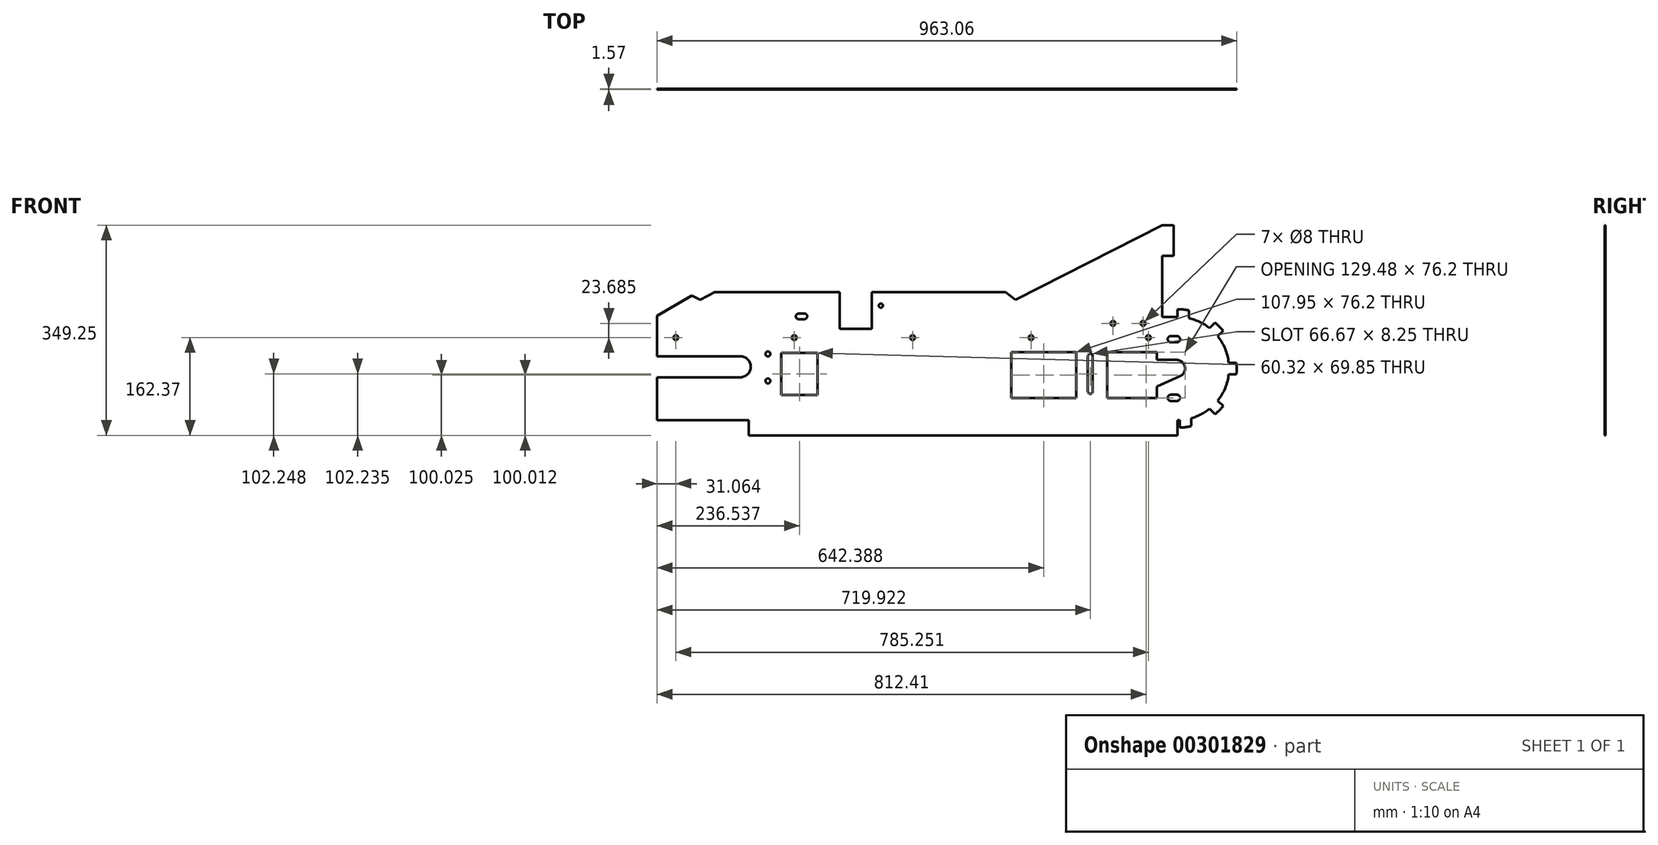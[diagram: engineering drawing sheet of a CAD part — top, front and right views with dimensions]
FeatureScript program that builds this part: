
annotation { "Feature Type Name" : "Feature", "Feature Type Description" : "" }
export const myFeature = defineFeature(function(context is Context, id is Id, definition is map)
    precondition{}
    {
        {
            var Q0;
            Q0=qCreatedBy(makeId("Front.planeOp"),FACE);
            var sketch = newSketch(context, id + "F0", { "sketchPlane" : qUnion([Q0])});
            skLineSegment(sketch, "E0", {"start": v(0, 0) * mm, "end": v(864.64, 0) * mm});
            skLineSegment(sketch, "E1", {"start": v(0, 71.12) * mm, "end": v(138.11, 71.12) * mm});
            skLineSegment(sketch, "E2", {"start": v(138.11, 106.05) * mm, "end": v(0, 106.05) * mm});
            skLineSegment(sketch, "E3", {"start": v(0, 106.05) * mm, "end": v(0, 158.75) * mm});
            skLineSegment(sketch, "E4", {"start": v(0, 158.75) * mm, "end": v(71.5, 200.03) * mm});
            skLineSegment(sketch, "E5", {"start": v(71.5, 200.03) * mm, "end": v(303.21, 200.03) * mm});
            skLineSegment(sketch, "E6", {"start": v(839.24, 323.85) * mm, "end": v(839.24, 171.45) * mm});
            skPoint(sketch, "E7", {"position": v(864.64, 85.73) * mm});
            skArc(sketch, "E8", {"start": v(864.64, 0) * mm, "mid": v(950.36, 85.73) * mm, "end": v(864.64, 171.45) * mm});
            skLineSegment(sketch, "E9", {"start": v(864.64, 171.45) * mm, "end": v(749.53, 171.45) * mm});
            skPoint(sketch, "E10", {"position": v(138.11, 88.58) * mm});
            skPoint(sketch, "E10.positionSnap0", {"position": v(155.58, 88.58) * mm});
            skArc(sketch, "E11", {"start": v(138.11, 71.12) * mm, "mid": v(155.58, 88.58) * mm, "end": v(138.11, 106.04) * mm});
            skLineSegment(sketch, "E12", {"start": v(206.38, 88.58) * mm, "end": v(206.38, 41.91) * mm});
            skLineSegment(sketch, "E13", {"start": v(206.38, 41.91) * mm, "end": v(266.7, 41.91) * mm});
            skLineSegment(sketch, "E14", {"start": v(266.7, 41.91) * mm, "end": v(266.7, 111.76) * mm});
            skLineSegment(sketch, "E15", {"start": v(266.7, 111.76) * mm, "end": v(206.38, 111.76) * mm});
            skLineSegment(sketch, "E16", {"start": v(206.38, 111.76) * mm, "end": v(206.38, 88.58) * mm});
            skLineSegment(sketch, "E17", {"start": v(0, 0) * mm, "end": v(0, 71.12) * mm});
            skPoint(sketch, "E18.orphan", {"position": v(155.58, 106.05) * mm});
            skPoint(sketch, "E19.orphan", {"position": v(155.57, 71.12) * mm});
            skLineSegment(sketch, "E20.bottom", {"start": v(747.67, 36.51) * mm, "end": v(830.22, 36.51) * mm});
            skLineSegment(sketch, "E20.top", {"start": v(747.67, 112.71) * mm, "end": v(830.22, 112.71) * mm});
            skLineSegment(sketch, "E20.left", {"start": v(747.67, 36.51) * mm, "end": v(747.67, 112.71) * mm});
            skLineSegment(sketch, "E20.right", {"start": v(830.22, 36.51) * mm, "end": v(830.22, 55.56) * mm});
            skLineSegment(sketch, "E21", {"start": v(830.22, 100.01) * mm, "end": v(862.98, 100.01) * mm});
            skPoint(sketch, "E22", {"position": v(830.22, 55.56) * mm});
            skPoint(sketch, "E23", {"position": v(862.98, 85.73) * mm});
            skArc(sketch, "E24", {"start": v(868.78, 72.66) * mm, "mid": v(876.96, 88.69) * mm, "end": v(862.98, 100.01) * mm});
            skLineSegment(sketch, "E25", {"start": v(830.22, 55.56) * mm, "end": v(868.78, 72.66) * mm});
            skLineSegment(sketch, "E26.trimOffspring", {"start": v(830.22, 100.01) * mm, "end": v(830.22, 112.71) * mm});
            skLineSegment(sketch, "E27", {"start": v(152.4, 0) * mm, "end": v(152.4, -25.4) * mm});
            skLineSegment(sketch, "E28", {"start": v(152.4, -25.4) * mm, "end": v(864.64, -25.4) * mm});
            skLineSegment(sketch, "E29", {"start": v(864.64, -25.4) * mm, "end": v(864.64, 0) * mm});
            skLineSegment(sketch, "E30", {"start": v(71.5, 200.03) * mm, "end": v(95.54, 212.72) * mm});
            skLineSegment(sketch, "E31", {"start": v(95.54, 212.72) * mm, "end": v(303.21, 212.72) * mm});
            skArc(sketch, "E32.0", {"start": v(868.87, -12.6) * mm, "mid": v(878.37, -11.74) * mm, "end": v(887.74, -9.95) * mm});
            skLineSegment(sketch, "E33", {"start": v(864.64, 184.15) * mm, "end": v(864.64, 171.45) * mm});
            skLineSegment(sketch, "E34", {"start": v(883.57, 169.33) * mm, "end": v(883.6, 182.3) * mm});
            skLineSegment(sketch, "E35", {"start": v(949.83, 95.25) * mm, "end": v(962.6, 95.25) * mm});
            skLineSegment(sketch, "E36", {"start": v(949.83, 76.2) * mm, "end": v(962.6, 76.2) * mm});
            skLineSegment(sketch, "E37", {"start": v(868.87, 0.1) * mm, "end": v(868.87, -12.6) * mm});
            skLineSegment(sketch, "E38", {"start": v(887.68, 3.15) * mm, "end": v(887.74, -9.95) * mm});
            skLineSegment(sketch, "E39", {"start": v(864.64, 85.73) * mm, "end": v(1016.4, 85.73) * mm});
            skLineSegment(sketch, "E40", {"start": v(864.64, 85.72) * mm, "end": v(975.8, 196.9) * mm});
            skLineSegment(sketch, "E41", {"start": v(864.64, 85.73) * mm, "end": v(950.36, 0) * mm});
            skLineSegment(sketch, "E42", {"start": v(918.14, 152.7) * mm, "end": v(927.17, 161.73) * mm});
            skLineSegment(sketch, "E43", {"start": v(931.61, 139.23) * mm, "end": v(940.64, 148.26) * mm});
            skLineSegment(sketch, "E44", {"start": v(931.61, 32.22) * mm, "end": v(940.64, 23.19) * mm});
            skLineSegment(sketch, "E45", {"start": v(918.14, 18.75) * mm, "end": v(927.17, 9.72) * mm});
            skArc(sketch, "E46.trimOffspring", {"start": v(927.17, 9.72) * mm, "mid": v(934.24, 16.13) * mm, "end": v(940.64, 23.19) * mm});
            skArc(sketch, "E47.trimOffspring", {"start": v(962.6, 76.2) * mm, "mid": v(962.95, 80.96) * mm, "end": v(963.06, 85.73) * mm});
            skArc(sketch, "E48.trimOffspring", {"start": v(940.64, 148.26) * mm, "mid": v(934.24, 155.32) * mm, "end": v(927.17, 161.73) * mm});
            skArc(sketch, "E49.trimOffspring", {"start": v(883.6, 182.3) * mm, "mid": v(874.16, 183.69) * mm, "end": v(864.64, 184.15) * mm});
            skLineSegment(sketch, "E50.0", {"start": v(0, 173.41) * mm, "end": v(57.89, 206.84) * mm});
            skLineSegment(sketch, "E51", {"start": v(71.5, 200.03) * mm, "end": v(57.89, 206.84) * mm});
            skLineSegment(sketch, "E52", {"start": v(0, 158.75) * mm, "end": v(0, 173.41) * mm});
            skLineSegment(sketch, "E53", {"start": v(439.73, 200.03) * mm, "end": v(455.23, 200.03) * mm});
            skLineSegment(sketch, "E54.bottom", {"start": v(839.24, 323.85) * mm, "end": v(858.29, 323.85) * mm});
            skLineSegment(sketch, "E54.top", {"start": v(839.24, 273.05) * mm, "end": v(858.29, 273.05) * mm});
            skLineSegment(sketch, "E54.left", {"start": v(839.24, 323.85) * mm, "end": v(839.24, 273.05) * mm});
            skLineSegment(sketch, "E54.right", {"start": v(858.29, 323.85) * mm, "end": v(858.29, 273.05) * mm});
            skLineSegment(sketch, "E55.bottom", {"start": v(839.24, 171.45) * mm, "end": v(858.29, 171.45) * mm});
            skLineSegment(sketch, "E55.top", {"start": v(839.24, 222.25) * mm, "end": v(858.29, 222.25) * mm});
            skLineSegment(sketch, "E55.left", {"start": v(839.24, 171.45) * mm, "end": v(839.24, 222.25) * mm});
            skLineSegment(sketch, "E55.right", {"start": v(858.29, 171.45) * mm, "end": v(858.29, 222.25) * mm});
            skLineSegment(sketch, "E56.bottom", {"start": v(696.36, 112.73) * mm, "end": v(588.41, 112.73) * mm});
            skLineSegment(sketch, "E56.top", {"start": v(696.36, 36.53) * mm, "end": v(588.41, 36.53) * mm});
            skLineSegment(sketch, "E56.left", {"start": v(696.36, 112.73) * mm, "end": v(696.36, 36.53) * mm});
            skLineSegment(sketch, "E56.right", {"start": v(588.41, 112.73) * mm, "end": v(588.41, 36.53) * mm});
            skLineSegment(sketch, "E57", {"start": v(719.92, 106.06) * mm, "end": v(719.92, 47.64) * mm});
            skArc(sketch, "E58", {"start": v(724.05, 106.06) * mm, "mid": v(719.92, 110.19) * mm, "end": v(715.8, 106.06) * mm});
            skCircle(sketch, "E59", {"center": v(719.92, 47.64) * mm, "radius": 4.13 * mm});
            skLineSegment(sketch, "E60", {"start": v(724.05, 106.06) * mm, "end": v(724.05, 47.64) * mm});
            skLineSegment(sketch, "E61", {"start": v(715.8, 106.06) * mm, "end": v(715.8, 47.64) * mm});
            skCircle(sketch, "E62", {"center": v(184.09, 109.82) * mm, "radius": 4.13 * mm});
            skCircle(sketch, "E63", {"center": v(184.09, 65.09) * mm, "radius": 4.13 * mm});
            skCircle(sketch, "E64", {"center": v(227.84, 136.97) * mm, "radius": 4 * mm});
            skLineSegment(sketch, "E65", {"start": v(303.21, 212.72) * mm, "end": v(303.21, 151.77) * mm});
            skLineSegment(sketch, "E66", {"start": v(356.55, 212.72) * mm, "end": v(356.55, 151.77) * mm});
            skLineSegment(sketch, "E67", {"start": v(356.55, 151.77) * mm, "end": v(303.21, 151.77) * mm});
            skPoint(sketch, "E68", {"position": v(595.31, 200.03) * mm});
            skLineSegment(sketch, "E69", {"start": v(595.31, 200.03) * mm, "end": v(839.24, 323.85) * mm});
            skLineSegment(sketch, "E70.trimOffspring", {"start": v(356.55, 200.03) * mm, "end": v(595.31, 200.03) * mm});
            skLineSegment(sketch, "E71.trimOffspring", {"start": v(356.55, 212.72) * mm, "end": v(579.16, 212.72) * mm});
            skLineSegment(sketch, "E72", {"start": v(595.31, 200.03) * mm, "end": v(579.16, 212.72) * mm});
            skCircle(sketch, "E73", {"center": v(757.51, 160.66) * mm, "radius": 4 * mm});
            skCircle(sketch, "E74", {"center": v(816.31, 137.03) * mm, "radius": 4 * mm});
            skCircle(sketch, "E75", {"center": v(807.58, 160.66) * mm, "radius": 4 * mm});
            skCircle(sketch, "E76", {"center": v(853.65, 134.37) * mm, "radius": 5.14 * mm});
            skCircle(sketch, "E77", {"center": v(863.94, 134.37) * mm, "radius": 5.14 * mm});
            skPoint(sketch, "E78", {"position": v(853.65, 36.96) * mm});
            skCircle(sketch, "E79", {"center": v(853.65, 36.96) * mm, "radius": 5.14 * mm});
            skCircle(sketch, "E80", {"center": v(863.94, 36.96) * mm, "radius": 5.14 * mm});
            skLineSegment(sketch, "E81", {"start": v(863.94, 42.1) * mm, "end": v(853.65, 42.1) * mm});
            skLineSegment(sketch, "E82", {"start": v(863.94, 31.81) * mm, "end": v(853.65, 31.81) * mm});
            skLineSegment(sketch, "E83", {"start": v(853.65, 139.5) * mm, "end": v(863.94, 139.5) * mm});
            skLineSegment(sketch, "E84", {"start": v(853.65, 129.22) * mm, "end": v(863.94, 129.22) * mm});
            skCircle(sketch, "E85", {"center": v(31.06, 136.97) * mm, "radius": 4 * mm});
            skCircle(sketch, "E86", {"center": v(424.61, 136.97) * mm, "radius": 4 * mm});
            skCircle(sketch, "E87", {"center": v(621.39, 136.97) * mm, "radius": 4 * mm});
            skCircle(sketch, "E88", {"center": v(244.67, 172.34) * mm, "radius": 4.7 * mm});
            skCircle(sketch, "E89", {"center": v(235.27, 172.34) * mm, "radius": 4.7 * mm});
            skLineSegment(sketch, "E90", {"start": v(244.67, 177.04) * mm, "end": v(235.27, 177.04) * mm});
            skLineSegment(sketch, "E91", {"start": v(244.67, 167.64) * mm, "end": v(235.27, 167.64) * mm});
            skCircle(sketch, "E92", {"center": v(371.8, 190.12) * mm, "radius": 3.43 * mm});
            skLineSegment(sketch, "E93", {"start": v(963.06, 85.73) * mm, "end": v(962.6, 95.25) * mm});
            skSolve(sketch);
        }
        {
            var Q0;
            Q0=makeQuery(id+"F0.imprint","IMPRINT",FACE,{"disambiguationData":[TD([[makeQuery(id+"F0.imprint","IMPRINT",EDGE,{"derivedFrom":sQuery(id+"F0.wireOp",EDGE,"E1")}),-1.0]])]});
            var Q1;
            {var subQ0=sQuery(id+"F0.wireOp",EDGE,"E8");var subQ8=makeQuery(id+"F0.imprint","INTERSECT",VERTEX,{"derivedFrom":[subQ0,sQuery(id+"F0.wireOp",EDGE,"E35")]});Q1=makeQuery(id+"F0.imprint","IMPRINT",FACE,{"disambiguationData":[TD([[makeQuery(id+"F0.imprint","IMPRINT",EDGE,{"disambiguationData":[TD([[subQ8,1.0]])],"derivedFrom":subQ0}),1.0]])]});}
            var Q2;
            {var subQ5=sQuery(id+"F0.wireOp",EDGE,"E8");var subQ7=makeQuery(id+"F0.imprint","INTERSECT",VERTEX,{"derivedFrom":[subQ5,sQuery(id+"F0.wireOp",EDGE,"E44")]});Q2=makeQuery(id+"F0.imprint","IMPRINT",FACE,{"disambiguationData":[TD([[makeQuery(id+"F0.imprint","IMPRINT",EDGE,{"disambiguationData":[TD([[subQ7,1.0]])],"derivedFrom":subQ5}),1.0]])]});}
            var Q3;
            {var subQ0=sQuery(id+"F0.wireOp",EDGE,"E36");Q3=makeQuery(id+"F0.imprint","IMPRINT",FACE,{"disambiguationData":[TD([[makeQuery(id+"F0.imprint","IMPRINT",EDGE,{"derivedFrom":subQ0}),1.0]])]});}
            var Q4;
            {var subQ0=sQuery(id+"F0.wireOp",EDGE,"E35");Q4=makeQuery(id+"F0.imprint","IMPRINT",FACE,{"disambiguationData":[TD([[makeQuery(id+"F0.imprint","IMPRINT",EDGE,{"derivedFrom":subQ0}),-1.0]])]});}
            var Q5;
            {var subQ0=sQuery(id+"F0.wireOp",EDGE,"E43");Q5=makeQuery(id+"F0.imprint","IMPRINT",FACE,{"disambiguationData":[TD([[makeQuery(id+"F0.imprint","IMPRINT",EDGE,{"derivedFrom":subQ0}),1.0]])]});}
            var Q6;
            {var subQ0=sQuery(id+"F0.wireOp",EDGE,"E42");Q6=makeQuery(id+"F0.imprint","IMPRINT",FACE,{"disambiguationData":[TD([[makeQuery(id+"F0.imprint","IMPRINT",EDGE,{"derivedFrom":subQ0}),-1.0]])]});}
            var Q7;
            {var subQ0=sQuery(id+"F0.wireOp",EDGE,"E33");Q7=makeQuery(id+"F0.imprint","IMPRINT",FACE,{"disambiguationData":[TD([[makeQuery(id+"F0.imprint","IMPRINT",EDGE,{"derivedFrom":subQ0}),1.0]])]});}
            var Q8;
            {var subQ0=sQuery(id+"F0.wireOp",EDGE,"E44");Q8=makeQuery(id+"F0.imprint","IMPRINT",FACE,{"disambiguationData":[TD([[makeQuery(id+"F0.imprint","IMPRINT",EDGE,{"derivedFrom":subQ0}),-1.0]])]});}
            var Q9;
            {var subQ0=sQuery(id+"F0.wireOp",EDGE,"E45");Q9=makeQuery(id+"F0.imprint","IMPRINT",FACE,{"disambiguationData":[TD([[makeQuery(id+"F0.imprint","IMPRINT",EDGE,{"derivedFrom":subQ0}),1.0]])]});}
            var Q10;
            Q10=makeQuery(id+"F0.imprint","IMPRINT",FACE,{"disambiguationData":[TD([[makeQuery(id+"F0.imprint","IMPRINT",EDGE,{"derivedFrom":sQuery(id+"F0.wireOp",EDGE,"E32.0")}),1.0]])]});
            var Q11;
            {var subQ2=sQuery(id+"F0.wireOp",EDGE,"E27");Q11=makeQuery(id+"F0.imprint","IMPRINT",FACE,{"disambiguationData":[TD([[makeQuery(id+"F0.imprint","IMPRINT",EDGE,{"derivedFrom":subQ2}),1.0]])]});}
            var Q12;
            Q12=makeQuery(id+"F0.imprint","IMPRINT",FACE,{"disambiguationData":[TD([[makeQuery(id+"F0.imprint","IMPRINT",EDGE,{"derivedFrom":sQuery(id+"F0.wireOp",EDGE,"E55.bottom")}),1.0]])]});
            var Q13;
            Q13=makeQuery(id+"F0.imprint","IMPRINT",FACE,{"disambiguationData":[TD([[makeQuery(id+"F0.imprint","IMPRINT",EDGE,{"derivedFrom":sQuery(id+"F0.wireOp",EDGE,"E54.bottom")}),-1.0]])]});
            var Q14;
            {var subQ6=sQuery(id+"F0.wireOp",EDGE,"E71.trimOffspring");Q14=makeQuery(id+"F0.imprint","IMPRINT",FACE,{"disambiguationData":[TD([[makeQuery(id+"F0.imprint","IMPRINT",EDGE,{"derivedFrom":subQ6}),-1.0]])]});}
            var Q15;
            {var subQ0=sQuery(id+"F0.wireOp",EDGE,"E5");Q15=makeQuery(id+"F0.imprint","IMPRINT",FACE,{"disambiguationData":[TD([[makeQuery(id+"F0.imprint","IMPRINT",EDGE,{"derivedFrom":subQ0}),1.0]])]});}
            var Q16;
            Q16=makeQuery(id+"F0.imprint","IMPRINT",FACE,{"disambiguationData":[TD([[makeQuery(id+"F0.imprint","IMPRINT",EDGE,{"derivedFrom":sQuery(id+"F0.wireOp",EDGE,"E4")}),1.0]])]});
            extrude(context, id + "F1", {"entities" : qUnion([Q0, Q1, Q2, Q3, Q4, Q5, Q6, Q7, Q8, Q9, Q10, Q11, Q12, Q13, Q14, Q15, Q16]), "depth" : 1.57 * mm});
        }
        {
            var Q0;
            Q0=makeQuery(id+"F1.opExtrude","CAP_FACE",FACE,{"disambiguationData":[OSD([sQuery(id+"F0.wireOp",EDGE,"E0"),sQuery(id+"F0.wireOp",EDGE,"E1"),sQuery(id+"F0.wireOp",EDGE,"E2"),sQuery(id+"F0.wireOp",EDGE,"E3"),sQuery(id+"F0.wireOp",EDGE,"E6"),sQuery(id+"F0.wireOp",EDGE,"E8"),sQuery(id+"F0.wireOp",EDGE,"E9"),sQuery(id+"F0.wireOp",EDGE,"E11"),sQuery(id+"F0.wireOp",EDGE,"E12"),sQuery(id+"F0.wireOp",EDGE,"E13"),sQuery(id+"F0.wireOp",EDGE,"E14"),sQuery(id+"F0.wireOp",EDGE,"E15"),sQuery(id+"F0.wireOp",EDGE,"E16"),sQuery(id+"F0.wireOp",EDGE,"E17"),sQuery(id+"F0.wireOp",EDGE,"E20.bottom"),sQuery(id+"F0.wireOp",EDGE,"E20.top"),sQuery(id+"F0.wireOp",EDGE,"E20.left"),sQuery(id+"F0.wireOp",EDGE,"E20.right"),sQuery(id+"F0.wireOp",EDGE,"E21"),sQuery(id+"F0.wireOp",EDGE,"E24"),sQuery(id+"F0.wireOp",EDGE,"E25"),sQuery(id+"F0.wireOp",EDGE,"E26.trimOffspring"),sQuery(id+"F0.wireOp",EDGE,"E27"),sQuery(id+"F0.wireOp",EDGE,"E28"),sQuery(id+"F0.wireOp",EDGE,"E29"),sQuery(id+"F0.wireOp",EDGE,"E30"),sQuery(id+"F0.wireOp",EDGE,"E31"),sQuery(id+"F0.wireOp",EDGE,"E32.0"),sQuery(id+"F0.wireOp",EDGE,"E33"),sQuery(id+"F0.wireOp",EDGE,"E34"),sQuery(id+"F0.wireOp",EDGE,"E35"),sQuery(id+"F0.wireOp",EDGE,"E36"),sQuery(id+"F0.wireOp",EDGE,"E37"),sQuery(id+"F0.wireOp",EDGE,"E38"),sQuery(id+"F0.wireOp",EDGE,"E42"),sQuery(id+"F0.wireOp",EDGE,"E43"),sQuery(id+"F0.wireOp",EDGE,"E44"),sQuery(id+"F0.wireOp",EDGE,"E45"),sQuery(id+"F0.wireOp",EDGE,"E46.trimOffspring"),sQuery(id+"F0.wireOp",EDGE,"E47.trimOffspring"),sQuery(id+"F0.wireOp",EDGE,"E48.trimOffspring"),sQuery(id+"F0.wireOp",EDGE,"E49.trimOffspring"),sQuery(id+"F0.wireOp",EDGE,"E50.0"),sQuery(id+"F0.wireOp",EDGE,"E51"),sQuery(id+"F0.wireOp",EDGE,"E52"),sQuery(id+"F0.wireOp",EDGE,"E54.bottom"),sQuery(id+"F0.wireOp",EDGE,"E54.top"),sQuery(id+"F0.wireOp",EDGE,"E54.right"),sQuery(id+"F0.wireOp",EDGE,"E55.top"),sQuery(id+"F0.wireOp",EDGE,"E55.right"),sQuery(id+"F0.wireOp",EDGE,"E56.bottom"),sQuery(id+"F0.wireOp",EDGE,"E56.top"),sQuery(id+"F0.wireOp",EDGE,"E56.left"),sQuery(id+"F0.wireOp",EDGE,"E56.right"),sQuery(id+"F0.wireOp",EDGE,"E58"),sQuery(id+"F0.wireOp",EDGE,"E59"),sQuery(id+"F0.wireOp",EDGE,"E60"),sQuery(id+"F0.wireOp",EDGE,"E61"),sQuery(id+"F0.wireOp",EDGE,"E62"),sQuery(id+"F0.wireOp",EDGE,"E63"),sQuery(id+"F0.wireOp",EDGE,"E64"),sQuery(id+"F0.wireOp",EDGE,"E65"),sQuery(id+"F0.wireOp",EDGE,"E66"),sQuery(id+"F0.wireOp",EDGE,"E67"),sQuery(id+"F0.wireOp",EDGE,"E69"),sQuery(id+"F0.wireOp",EDGE,"E71.trimOffspring"),sQuery(id+"F0.wireOp",EDGE,"E72"),sQuery(id+"F0.wireOp",EDGE,"E73"),sQuery(id+"F0.wireOp",EDGE,"E74"),sQuery(id+"F0.wireOp",EDGE,"E75"),sQuery(id+"F0.wireOp",EDGE,"E76"),sQuery(id+"F0.wireOp",EDGE,"E77"),sQuery(id+"F0.wireOp",EDGE,"E79"),sQuery(id+"F0.wireOp",EDGE,"E80"),sQuery(id+"F0.wireOp",EDGE,"E81"),sQuery(id+"F0.wireOp",EDGE,"E82"),sQuery(id+"F0.wireOp",EDGE,"E83"),sQuery(id+"F0.wireOp",EDGE,"E84"),sQuery(id+"F0.wireOp",EDGE,"E85"),sQuery(id+"F0.wireOp",EDGE,"E86"),sQuery(id+"F0.wireOp",EDGE,"E87"),sQuery(id+"F0.wireOp",EDGE,"E88"),sQuery(id+"F0.wireOp",EDGE,"E89"),sQuery(id+"F0.wireOp",EDGE,"E90"),sQuery(id+"F0.wireOp",EDGE,"E91"),sQuery(id+"F0.wireOp",EDGE,"E92"),sQuery(id+"F0.wireOp",EDGE,"E93")])],"isStart":false});
            var sketch = newSketch(context, id + "F2", { "sketchPlane" : qUnion([Q0])});
            skLineSegment(sketch, "E94.bottom", {"start": v(858.29, 171.45) * mm, "end": v(839.24, 171.45) * mm});
            skLineSegment(sketch, "E94.top", {"start": v(858.29, 173.02) * mm, "end": v(839.24, 173.02) * mm});
            skLineSegment(sketch, "E94.left", {"start": v(858.29, 171.45) * mm, "end": v(858.29, 173.02) * mm});
            skLineSegment(sketch, "E94.right", {"start": v(839.24, 171.45) * mm, "end": v(839.24, 173.02) * mm});
            skSolve(sketch);
        }
        {
            var Q0;
            Q0=makeQuery(id+"F2.imprint","IMPRINT",FACE,{"disambiguationData":[TD([[makeQuery(id+"F2.imprint","IMPRINT",EDGE,{"derivedFrom":sQuery(id+"F2.wireOp",EDGE,"E94.bottom")}),-1.0]])]});
            extrude(context, id + "F3", {"entities" : qUnion([Q0]), "operationType" : NewBodyOperationType.REMOVE, "oppositeDirection" : true, "depth" : 25.4 * mm});
        }
    });
